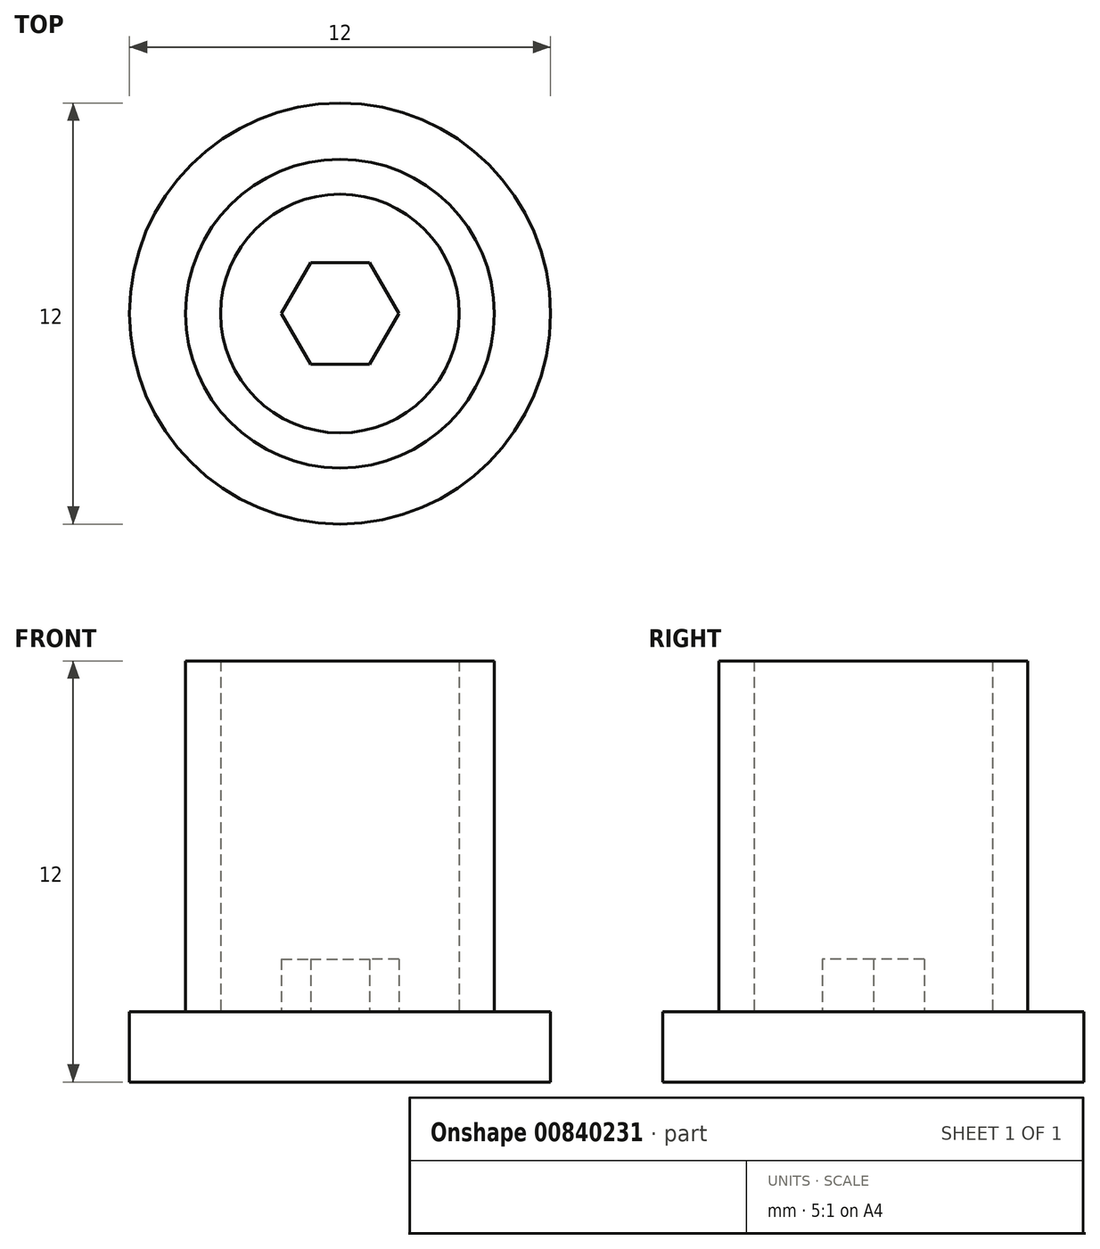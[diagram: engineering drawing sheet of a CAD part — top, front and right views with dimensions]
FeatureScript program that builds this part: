
annotation { "Feature Type Name" : "Feature", "Feature Type Description" : "" }
export const myFeature = defineFeature(function(context is Context, id is Id, definition is map)
    precondition{}
    {
        {
            var Q0;
            Q0=qCreatedBy(makeId("Top.planeOp"),FACE);
            var sketch = newSketch(context, id + "F0", { "sketchPlane" : qUnion([Q0])});
            skCircle(sketch, "E0", {"center": v(0, 0) * mm, "radius": 6 * mm});
            skCircle(sketch, "E1", {"center": v(0, 0) * mm, "radius": 3.4 * mm});
            skCircle(sketch, "E2", {"center": v(0, 0) * mm, "radius": 4.4 * mm});
            skCircle(sketch, "E3.cCircle", {"center": v(0, 0) * mm, "radius": 1.45 * mm, "construction": true});
            skLineSegment(sketch, "E3.0", {"start": v(1.67, 0) * mm, "end": v(0.84, -1.45) * mm});
            skLineSegment(sketch, "E3.1", {"start": v(0.84, -1.45) * mm, "end": v(-0.84, -1.45) * mm});
            skLineSegment(sketch, "E3.2", {"start": v(-0.84, -1.45) * mm, "end": v(-1.67, 0) * mm});
            skLineSegment(sketch, "E3.3", {"start": v(-1.67, 0) * mm, "end": v(-0.84, 1.45) * mm});
            skLineSegment(sketch, "E3.4", {"start": v(-0.84, 1.45) * mm, "end": v(0.84, 1.45) * mm});
            skLineSegment(sketch, "E3.5", {"start": v(0.84, 1.45) * mm, "end": v(1.67, 0) * mm});
            skPoint(sketch, "E3.0.midPoint", {"position": v(1.26, -0.72) * mm});
            skSolve(sketch);
        }
        {
            var Q0;
            Q0=makeQuery(id+"F0.imprint","IMPRINT",FACE,{"disambiguationData":[TD([[makeQuery(id+"F0.imprint","IMPRINT",EDGE,{"derivedFrom":sQuery(id+"F0.wireOp",EDGE,"E0")}),1.0]])]});
            var Q1;
            Q1=makeQuery(id+"F0.imprint","IMPRINT",FACE,{"disambiguationData":[TD([[makeQuery(id+"F0.imprint","IMPRINT",EDGE,{"derivedFrom":sQuery(id+"F0.wireOp",EDGE,"E1")}),-1.0]])]});
            var Q2;
            Q2=makeQuery(id+"F0.imprint","IMPRINT",FACE,{"disambiguationData":[TD([[makeQuery(id+"F0.imprint","IMPRINT",EDGE,{"derivedFrom":sQuery(id+"F0.wireOp",EDGE,"E1")}),1.0]])]});
            extrude(context, id + "F1", {"entities" : qUnion([Q0, Q1, Q2]), "oppositeDirection" : true, "depth" : 2 * mm});
        }
        {
            var Q0;
            Q0=makeQuery(id+"F0.imprint","IMPRINT",FACE,{"disambiguationData":[TD([[makeQuery(id+"F0.imprint","IMPRINT",EDGE,{"derivedFrom":sQuery(id+"F0.wireOp",EDGE,"E1")}),-1.0]])]});
            extrude(context, id + "F2", {"entities" : qUnion([Q0]), "operationType" : NewBodyOperationType.ADD, "depth" : 10 * mm});
        }
        {
            var Q0;
            Q0=makeQuery(id+"F0.imprint","IMPRINT",FACE,{"disambiguationData":[TD([[makeQuery(id+"F0.imprint","IMPRINT",EDGE,{"derivedFrom":sQuery(id+"F0.wireOp",EDGE,"E3.0")}),-1.0]])]});
            extrude(context, id + "F3", {"entities" : qUnion([Q0]), "operationType" : NewBodyOperationType.ADD, "depth" : 1.5 * mm});
        }
        {
            var Q0;
            Q0=makeQuery(id+"F3.opExtrude","CAP_FACE",FACE,{"disambiguationData":[OSD([sQuery(id+"F0.wireOp",EDGE,"E3.0"),sQuery(id+"F0.wireOp",EDGE,"E3.1"),sQuery(id+"F0.wireOp",EDGE,"E3.2"),sQuery(id+"F0.wireOp",EDGE,"E3.3"),sQuery(id+"F0.wireOp",EDGE,"E3.4"),sQuery(id+"F0.wireOp",EDGE,"E3.5")])],"isStart":true});
            extrude(context, id + "F4", {"entities" : qUnion([Q0]), "operationType" : NewBodyOperationType.ADD, "depth" : 2 * mm});
        }
    });
